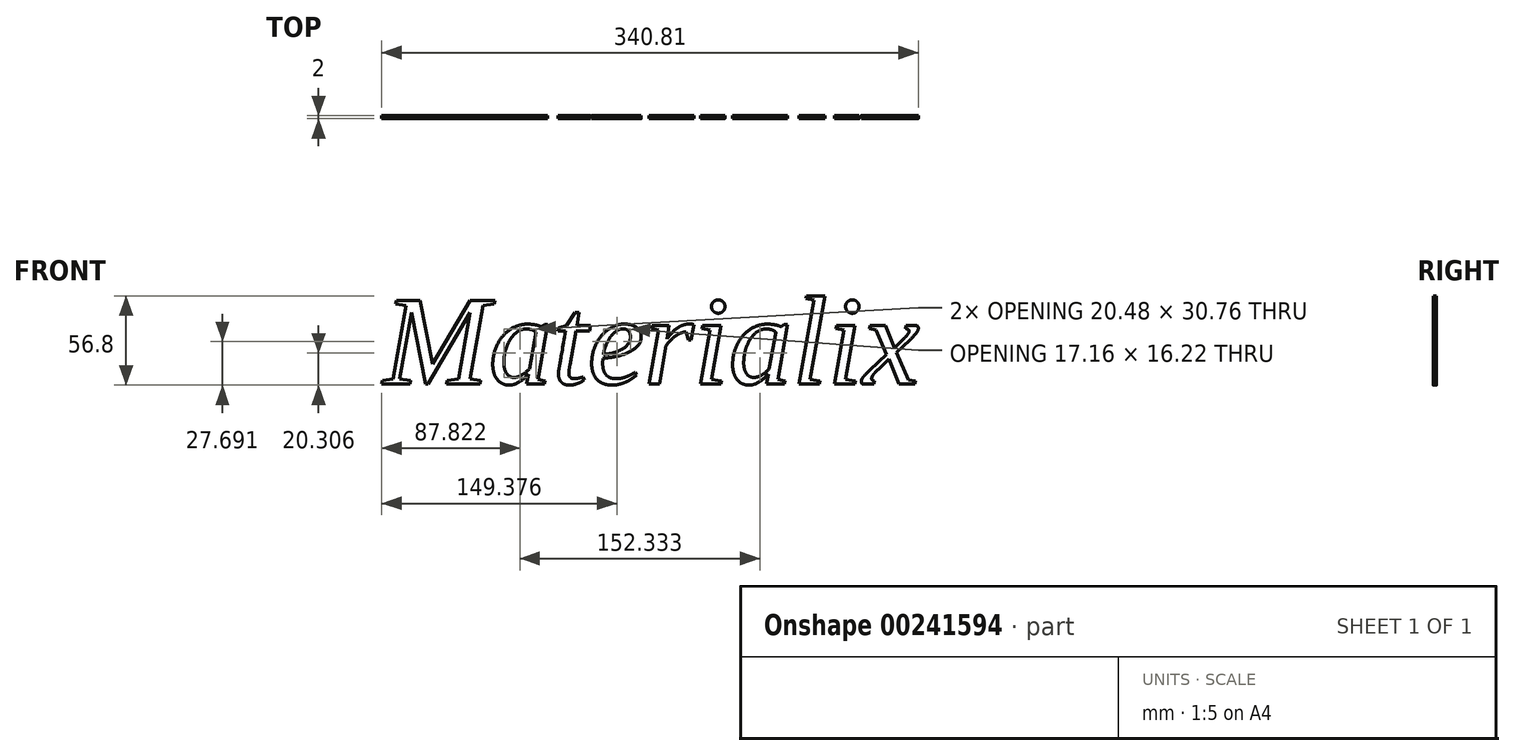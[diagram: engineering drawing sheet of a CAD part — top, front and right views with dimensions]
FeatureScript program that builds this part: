
annotation { "Feature Type Name" : "Feature", "Feature Type Description" : "" }
export const myFeature = defineFeature(function(context is Context, id is Id, definition is map)
    precondition{}
    {
        {
            var Q0;
            Q0=qCreatedBy(makeId("Front.planeOp"),FACE);
            var sketch = newSketch(context, id + "F0", { "sketchPlane" : qUnion([Q0])});
            skText(sketch, "E0", { "text": "Materialix", "fontName": "Tinos-Italic.ttf"});
            const initialGuessF0  = {"E0": [-0.0972, -0.02477, 1, 0, 0.05807]};
            skSetInitialGuess(sketch, initialGuessF0);
            skSolve(sketch);
        }
        {
            var Q0;
            Q0 = qSketchRegion(id + "F0", true);
            extrude(context, id + "F1", {"entities" : qUnion([Q0]), "depth" : 2 * mm});
        }
    });
